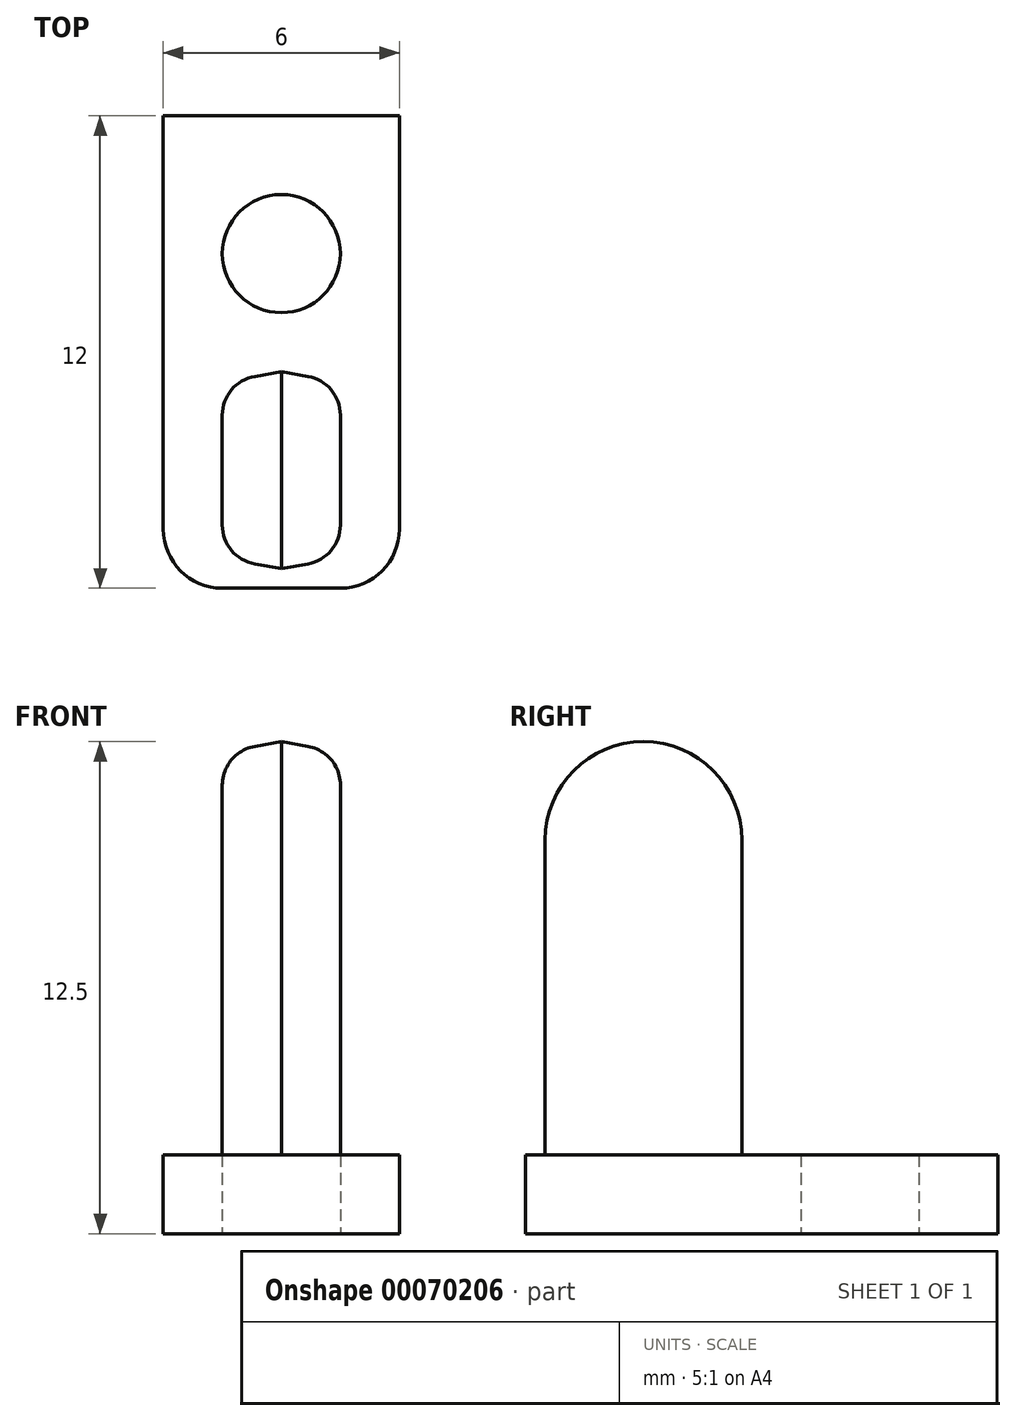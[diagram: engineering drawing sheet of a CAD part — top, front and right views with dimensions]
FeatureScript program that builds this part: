
annotation { "Feature Type Name" : "Feature", "Feature Type Description" : "" }
export const myFeature = defineFeature(function(context is Context, id is Id, definition is map)
    precondition{}
    {
        {
            var Q0;
            Q0=qCreatedBy(makeId("Right.planeOp"),FACE);
            var sketch = newSketch(context, id + "F0", { "sketchPlane" : qUnion([Q0])});
            skArc(sketch, "E0", {"start": v(0, 30) * mm, "mid": v(-10, 20) * mm, "end": v(0, 10) * mm});
            skLineSegment(sketch, "E1", {"start": v(0, 10) * mm, "end": v(0, 0) * mm});
            skArc(sketch, "E2.0.startCap", {"start": v(0, 32.5) * mm, "mid": v(2.5, 30) * mm, "end": v(0, 27.5) * mm});
            skArc(sketch, "E2.0.endCap", {"start": v(0, 12.5) * mm, "mid": v(2.5, 10) * mm, "end": v(0, 7.5) * mm});
            skArc(sketch, "E2.0.left", {"start": v(0, 27.5) * mm, "mid": v(-7.5, 20) * mm, "end": v(0, 12.5) * mm});
            skArc(sketch, "E2.0.right", {"start": v(0, 32.5) * mm, "mid": v(-12.5, 20) * mm, "end": v(0, 7.5) * mm});
            skArc(sketch, "E2.1.startCap", {"start": v(-2.5, 10) * mm, "mid": v(0, 12.5) * mm, "end": v(2.5, 10) * mm});
            skArc(sketch, "E2.1.endCap", {"start": v(2.5, 0) * mm, "mid": v(0, -2.5) * mm, "end": v(-2.5, 0) * mm});
            skLineSegment(sketch, "E2.1.left", {"start": v(2.5, 10) * mm, "end": v(2.5, 0) * mm});
            skLineSegment(sketch, "E2.1.right", {"start": v(-2.5, 10) * mm, "end": v(-2.5, 0) * mm});
            skLineSegment(sketch, "E3", {"start": v(-2.5, 0) * mm, "end": v(2.5, 0) * mm});
            skSolve(sketch);
        }
        {
            var Q0;
            {var subQ5=sQuery(id+"F0.wireOp",EDGE,"E2.0.startCap");Q0=makeQuery(id+"F0.imprint","IMPRINT",FACE,{"disambiguationData":[TD([[makeQuery(id+"F0.imprint","IMPRINT",EDGE,{"derivedFrom":subQ5}),-1.0]])]});}
            var Q1;
            {var subQ0=sQuery(id+"F0.wireOp",EDGE,"E3");var subQ1=sQuery(id+"F0.wireOp",EDGE,"E1");var subQ2=makeQuery(id+"F0.imprint","INTERSECT",VERTEX,{"derivedFrom":[subQ1,subQ0]});Q1=makeQuery(id+"F0.imprint","IMPRINT",FACE,{"disambiguationData":[TD([[makeQuery(id+"F0.imprint","IMPRINT",EDGE,{"disambiguationData":[TD([[subQ2,1.0]])],"derivedFrom":subQ1}),-1.0]])]});}
            var Q2;
            {var subQ3=sQuery(id+"F0.wireOp",EDGE,"E2.0.endCap");Q2=makeQuery(id+"F0.imprint","IMPRINT",FACE,{"disambiguationData":[TD([[makeQuery(id+"F0.imprint","IMPRINT",EDGE,{"derivedFrom":subQ3}),1.0]])]});}
            var Q3;
            {var subQ4=sQuery(id+"F0.wireOp",EDGE,"E2.0.endCap");Q3=makeQuery(id+"F0.imprint","IMPRINT",FACE,{"disambiguationData":[TD([[makeQuery(id+"F0.imprint","IMPRINT",EDGE,{"derivedFrom":subQ4}),-1.0]])]});}
            var Q4;
            {var subQ3=sQuery(id+"F0.wireOp",EDGE,"E0");var subQ5=sQuery(id+"F0.wireOp",EDGE,"E1");var subQ6=makeQuery(id+"F0.imprint","INTERSECT",VERTEX,{"derivedFrom":[subQ3,subQ5]});Q4=makeQuery(id+"F0.imprint","IMPRINT",FACE,{"disambiguationData":[TD([[makeQuery(id+"F0.imprint","IMPRINT",EDGE,{"disambiguationData":[TD([[subQ6,1.0]])],"derivedFrom":subQ3}),-1.0]])]});}
            extrude(context, id + "F1", {"entities" : qUnion([Q0, Q1, Q2, Q3, Q4]), "depth" : 3 * mm, "hasDraft" : true, "draftAngle" : 10 * degree, "draftPullDirection" : true, "symmetric" : true});
        }
        {
            var Q0;
            Q0=qCreatedBy(makeId("Top.planeOp"),FACE);
            var sketch = newSketch(context, id + "F2", { "sketchPlane" : qUnion([Q0])});
            skLineSegment(sketch, "E4.rect.bottom", {"start": v(1.5, -3) * mm, "end": v(-1.5, -3) * mm});
            skLineSegment(sketch, "E4.rect.top", {"start": v(3, 9) * mm, "end": v(-3, 9) * mm});
            skLineSegment(sketch, "E4.rect.left", {"start": v(3, -1.5) * mm, "end": v(3, 9) * mm});
            skLineSegment(sketch, "E4.rect.right", {"start": v(-3, -1.5) * mm, "end": v(-3, 9) * mm});
            skPoint(sketch, "E4.rect.middle", {"position": v(0, 3) * mm});
            skCircle(sketch, "E5", {"center": v(0, 5.5) * mm, "radius": 1.5 * mm});
            skPoint(sketch, "E6.visualSharp", {"position": v(3, -3) * mm});
            skArc(sketch, "E6.filletArc", {"start": v(1.5, -3) * mm, "mid": v(2.56, -2.56) * mm, "end": v(3, -1.5) * mm});
            skPoint(sketch, "E7.visualSharp", {"position": v(-3, -3) * mm});
            skArc(sketch, "E7.filletArc", {"start": v(-3, -1.5) * mm, "mid": v(-2.56, -2.56) * mm, "end": v(-1.5, -3) * mm});
            skSolve(sketch);
        }
        {
            var Q0;
            Q0=makeQuery(id+"F2.imprint","IMPRINT",FACE,{"disambiguationData":[TD([[makeQuery(id+"F2.imprint","IMPRINT",EDGE,{"derivedFrom":sQuery(id+"F2.wireOp",EDGE,"E4.rect.bottom")}),-1.0]])]});
            extrude(context, id + "F3", {"entities" : qUnion([Q0]), "operationType" : NewBodyOperationType.ADD, "depth" : 2 * mm});
        }
        {
            var Q0;
            Q0=makeQuery(id+"F1.opExtrude","CAP_EDGE",EDGE,{"disambiguationData":[OSD([sQuery(id+"F0.wireOp",EDGE,"E2.1.left")])],"isStart":true});
            var Q1;
            Q1=makeQuery(id+"F1.opExtrude","CAP_EDGE",EDGE,{"disambiguationData":[OSD([sQuery(id+"F0.wireOp",EDGE,"E2.1.left")])],"isStart":false});
            var Q2;
            Q2=makeQuery(id+"F1.opExtrude","CAP_EDGE",EDGE,{"disambiguationData":[OSD([sQuery(id+"F0.wireOp",EDGE,"E2.1.right")])],"isStart":false});
            var Q3;
            Q3=makeQuery(id+"F1.opExtrude","CAP_EDGE",EDGE,{"disambiguationData":[OSD([sQuery(id+"F0.wireOp",EDGE,"E2.1.right")])],"isStart":true});
            fillet(context, id + "F4", {"entities" : qUnion([Q0, Q1, Q2, Q3]), "radius" : 1 * mm, "tangentPropagation" : true, "allowEdgeOverflow" : false});
        }
    });
